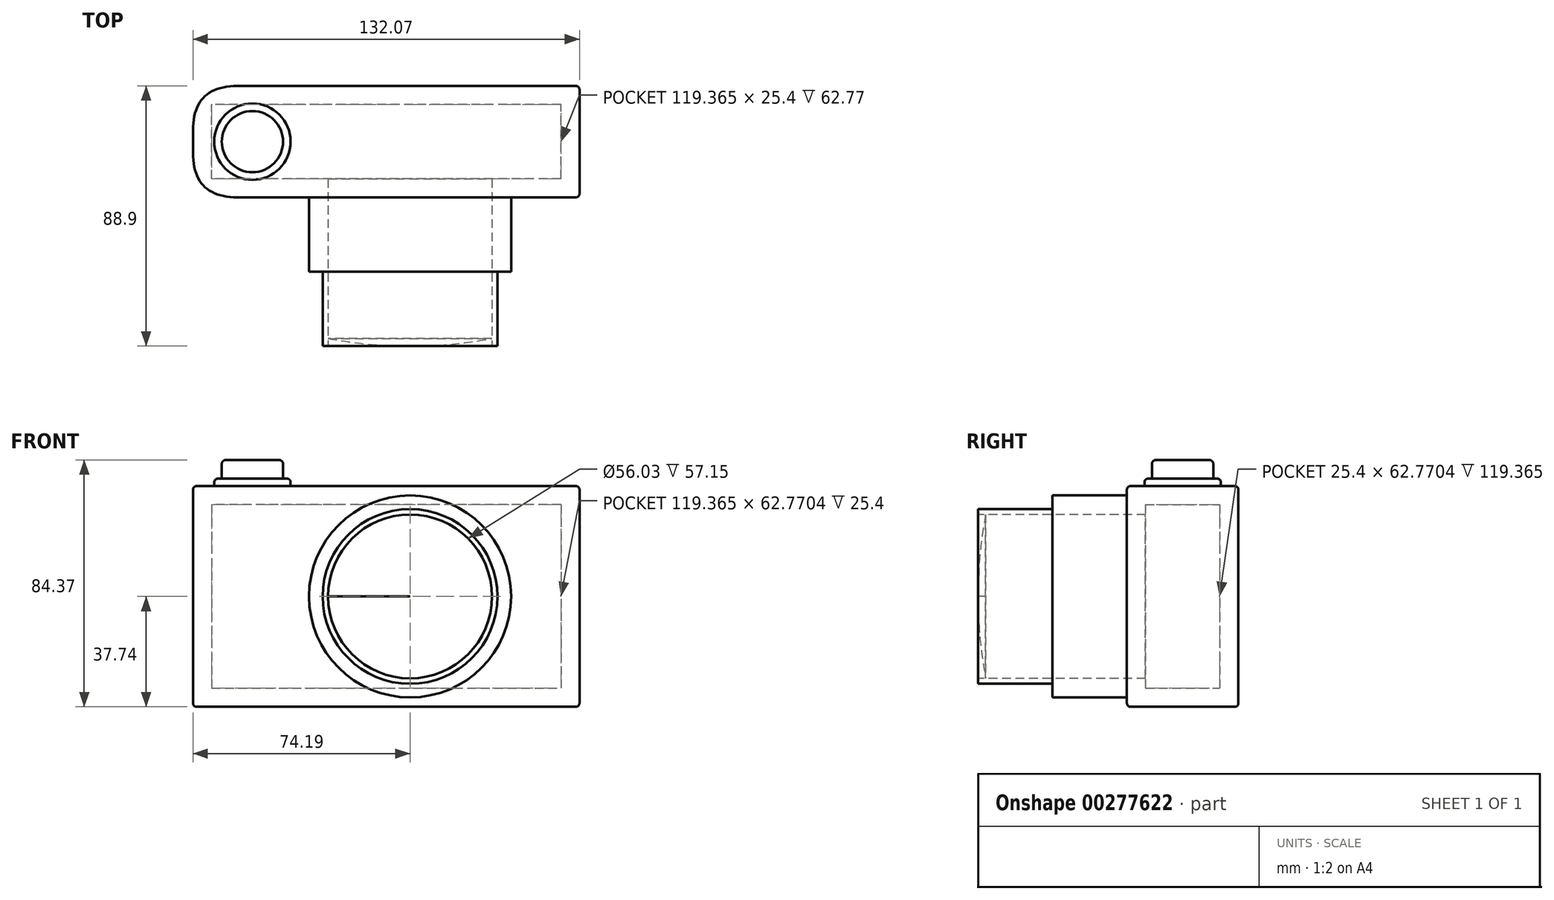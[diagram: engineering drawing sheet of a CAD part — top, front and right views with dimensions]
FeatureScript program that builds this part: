
annotation { "Feature Type Name" : "Feature", "Feature Type Description" : "" }
export const myFeature = defineFeature(function(context is Context, id is Id, definition is map)
    precondition{}
    {
        {
            var Q0;
            Q0=qCreatedBy(makeId("Front.planeOp"),FACE);
            var sketch = newSketch(context, id + "F0", { "sketchPlane" : qUnion([Q0])});
            skLineSegment(sketch, "E0.bottom", {"start": v(57.88, 37.74) * mm, "end": v(-57.88, 37.74) * mm});
            skLineSegment(sketch, "E0.top", {"start": v(57.88, -37.74) * mm, "end": v(-57.88, -37.74) * mm});
            skLineSegment(sketch, "E0.left", {"start": v(57.88, 37.74) * mm, "end": v(57.88, -37.74) * mm});
            skPoint(sketch, "E0.middle", {"position": v(0, 0) * mm});
            skCircle(sketch, "E1", {"center": v(0, 0) * mm, "radius": 34.52 * mm});
            skCircle(sketch, "E2", {"center": v(0, 0) * mm, "radius": 29.87 * mm});
            skLineSegment(sketch, "E3", {"start": v(-57.88, 37.74) * mm, "end": v(-74.19, 37.74) * mm});
            skLineSegment(sketch, "E4", {"start": v(-74.19, 37.74) * mm, "end": v(-74.19, -37.74) * mm});
            skLineSegment(sketch, "E5", {"start": v(-74.19, -37.74) * mm, "end": v(-57.88, -37.74) * mm});
            skSolve(sketch);
        }
        {
            var Q0;
            Q0 = qSketchRegion(id + "F0", true);
            var Q1;
            Q1=makeQuery(id+"F0.imprint","IMPRINT",FACE,{"disambiguationData":[TD([[makeQuery(id+"F0.imprint","IMPRINT",EDGE,{"derivedFrom":sQuery(id+"F0.wireOp",EDGE,"E1")}),1.0]])]});
            var Q2;
            Q2=makeQuery(id+"F0.imprint","IMPRINT",FACE,{"disambiguationData":[TD([[makeQuery(id+"F0.imprint","IMPRINT",EDGE,{"derivedFrom":sQuery(id+"F0.wireOp",EDGE,"E2")}),1.0]])]});
            extrude(context, id + "F1", {"entities" : qUnion([Q0, Q1, Q2]), "depth" : 38.1 * mm});
        }
        {
            var Q0;
            Q0=makeQuery(id+"F1.opExtrude","CAP_FACE",FACE,{"disambiguationData":[OSD([sQuery(id+"F0.wireOp",EDGE,"E0.bottom"),sQuery(id+"F0.wireOp",EDGE,"E0.top"),sQuery(id+"F0.wireOp",EDGE,"E0.left"),sQuery(id+"F0.wireOp",EDGE,"E3"),sQuery(id+"F0.wireOp",EDGE,"E4"),sQuery(id+"F0.wireOp",EDGE,"E5")])],"isStart":false});
            var Q1;
            Q1=makeQuery(id+"F1.opExtrude","SWEPT_BODY",BODY,{"disambiguationData":[OSD([sQuery(id+"F0.wireOp",EDGE,"E0.bottom"),sQuery(id+"F0.wireOp",EDGE,"E0.top"),sQuery(id+"F0.wireOp",EDGE,"E0.left"),sQuery(id+"F0.wireOp",EDGE,"E3"),sQuery(id+"F0.wireOp",EDGE,"E4"),sQuery(id+"F0.wireOp",EDGE,"E5")])]});
            shell(context, id + "F2", {"isHollow" : true, "entities" : qUnion([Q0]), "parts" : qUnion([Q1]), "thickness" : 6.35 * mm});
        }
        {
            var Q0;
            Q0=makeQuery(id+"F0.imprint","IMPRINT",FACE,{"disambiguationData":[TD([[makeQuery(id+"F0.imprint","IMPRINT",EDGE,{"derivedFrom":sQuery(id+"F0.wireOp",EDGE,"E1")}),1.0]])]});
            var Q1;
            Q1=makeQuery(id+"F0.imprint","IMPRINT",FACE,{"disambiguationData":[TD([[makeQuery(id+"F0.imprint","IMPRINT",EDGE,{"derivedFrom":sQuery(id+"F0.wireOp",EDGE,"E2")}),1.0]])]});
            extrude(context, id + "F3", {"entities" : qUnion([Q0, Q1]), "operationType" : NewBodyOperationType.ADD, "depth" : 63.5 * mm, "hasSecondDirection" : true, "secondDirectionOppositeDirection" : false, "secondDirectionDepth" : 38.1 * mm});
        }
        {
            var Q0;
            Q0=makeQuery(id+"F0.imprint","IMPRINT",FACE,{"disambiguationData":[TD([[makeQuery(id+"F0.imprint","IMPRINT",EDGE,{"derivedFrom":sQuery(id+"F0.wireOp",EDGE,"E2")}),1.0]])]});
            extrude(context, id + "F4", {"entities" : qUnion([Q0]), "operationType" : NewBodyOperationType.ADD, "depth" : 88.9 * mm, "hasSecondDirection" : true, "secondDirectionOppositeDirection" : false, "secondDirectionDepth" : 38.1 * mm});
        }
        {
            var Q0;
            Q0=makeQuery(id+"F1.opExtrude","SWEPT_FACE",FACE,{"disambiguationData":[OSD([sQuery(id+"F0.wireOp",EDGE,"E0.bottom"),sQuery(id+"F0.wireOp",EDGE,"E3")])]});
            var sketch = newSketch(context, id + "F5", { "sketchPlane" : qUnion([Q0])});
            skLineSegment(sketch, "E6.0", {"start": v(57.88, 0) * mm, "end": v(-74.19, 0) * mm});
            skLineSegment(sketch, "E7.0", {"start": v(-74.19, -38.1) * mm, "end": v(-74.19, 0) * mm});
            skLineSegment(sketch, "E8.0", {"start": v(57.88, -38.1) * mm, "end": v(-74.19, -38.1) * mm});
            skCircle(sketch, "E9", {"center": v(-53.87, -19.05) * mm, "radius": 13.04 * mm});
            skPoint(sketch, "E9.centerSnap0", {"position": v(-74.19, -19.05) * mm});
            skCircle(sketch, "E10", {"center": v(-53.87, -19.05) * mm, "radius": 10.45 * mm});
            skSolve(sketch);
        }
        {
            var Q0;
            Q0=makeQuery(id+"F5.imprint","IMPRINT",FACE,{"disambiguationData":[TD([[makeQuery(id+"F5.imprint","IMPRINT",EDGE,{"derivedFrom":sQuery(id+"F5.wireOp",EDGE,"E9")}),1.0]])]});
            extrude(context, id + "F6", {"entities" : qUnion([Q0]), "operationType" : NewBodyOperationType.ADD, "depth" : 2.54 * mm});
        }
        {
            var Q0;
            Q0=makeQuery(id+"F6.boolean.opBoolean","SPLIT",FACE,{"disambiguationData":[TD([makeQuery(id+"F6.opExtrude","SWEPT_FACE",FACE,{"disambiguationData":[OSD([sQuery(id+"F5.wireOp",EDGE,"E10")])]})])],"derivedFrom":makeQuery(id+"F1.opExtrude","SWEPT_FACE",FACE,{"disambiguationData":[OSD([sQuery(id+"F0.wireOp",EDGE,"E0.bottom"),sQuery(id+"F0.wireOp",EDGE,"E3")])]})});
            extrude(context, id + "F7", {"entities" : qUnion([Q0]), "operationType" : NewBodyOperationType.ADD, "depth" : 8.9 * mm});
        }
        {
            var Q0;
            Q0=makeQuery(id+"F4.opExtrude","CAP_FACE",FACE,{"disambiguationData":[OSD([sQuery(id+"F0.wireOp",EDGE,"E2")])],"isStart":false});
            var sketch = newSketch(context, id + "F8", { "sketchPlane" : qUnion([Q0])});
            skCircle(sketch, "E11", {"center": v(0, 0) * mm, "radius": 28.01 * mm});
            skSolve(sketch);
        }
        {
            var Q0;
            Q0=makeQuery(id+"F8.imprint","IMPRINT",FACE,{"disambiguationData":[TD([[makeQuery(id+"F8.imprint","IMPRINT",EDGE,{"derivedFrom":sQuery(id+"F8.wireOp",EDGE,"E11")}),1.0]])]});
            extrude(context, id + "F9", {"entities" : qUnion([Q0]), "operationType" : NewBodyOperationType.REMOVE, "oppositeDirection" : true, "depth" : 2.54 * mm});
        }
        {
            var Q0;
            Q0=qCreatedBy(makeId("Top.planeOp"),FACE);
            var sketch = newSketch(context, id + "F10", { "sketchPlane" : qUnion([Q0])});
            skLineSegment(sketch, "E12.0", {"start": v(28.01, -86.36) * mm, "end": v(-28.01, -86.36) * mm});
            skLineSegment(sketch, "E13.0", {"start": v(28.01, -88.9) * mm, "end": v(-28.01, -88.9) * mm});
            skFitSpline(sketch, "E14", {"points": [v(-28.01, -86.36) * mm, v(0, -88.9) * mm], "startDerivative": vector(28.09, -4.85) * mm, "endDerivative": vector(35.68, 0) * mm});
            skLineSegment(sketch, "E15", {"start": v(0, -88.9) * mm, "end": v(0, -86.36) * mm});
            skSolve(sketch);
        }
        {
            var Q0;
            Q0=makeQuery(id+"F8.imprint","IMPRINT",FACE,{"disambiguationData":[TD([[makeQuery(id+"F8.imprint","IMPRINT",EDGE,{"derivedFrom":sQuery(id+"F8.wireOp",EDGE,"E11")}),1.0]])]});
            extrude(context, id + "F11", {"entities" : qUnion([Q0]), "operationType" : NewBodyOperationType.REMOVE, "oppositeDirection" : true, "depth" : 63.5 * mm});
        }
        {
            var Q0;
            {var subQ0=sQuery(id+"F10.wireOp",EDGE,"E14");Q0=makeQuery(id+"F10.imprint","IMPRINT",FACE,{"disambiguationData":[TD([[makeQuery(id+"F10.imprint","IMPRINT",EDGE,{"derivedFrom":subQ0}),1.0]])]});}
            var Q1;
            Q1=sQuery(id+"F10.wireOp",EDGE,"E14");
            var Q2;
            Q2=sQuery(id+"F10.wireOp",EDGE,"E15");
            revolve(context, id + "F12", {"entities" : qUnion([Q0]), "surfaceEntities" : qUnion([Q1]), "axis" : qUnion([Q2]), "revolveType" : RevolveType.SYMMETRIC, "angle" : 360 * degree});
        }
        {
            var Q0;
            Q0=makeQuery(id+"F1.opExtrude","CAP_EDGE",EDGE,{"disambiguationData":[OSD([sQuery(id+"F0.wireOp",EDGE,"E4")])],"isStart":false});
            var Q1;
            Q1=makeQuery(id+"F1.opExtrude","CAP_EDGE",EDGE,{"disambiguationData":[OSD([sQuery(id+"F0.wireOp",EDGE,"E4")])],"isStart":true});
            fillet(context, id + "F13", {"entities" : qUnion([Q0, Q1]), "radius" : 15.24 * mm, "tangentPropagation" : true, "rho" : 0.5, "crossSection" : FilletCrossSection.CONIC, "allowEdgeOverflow" : false});
        }
        {
            var Q0;
            Q0=makeQuery(id+"F1.opExtrude","CAP_EDGE",EDGE,{"disambiguationData":[OSD([sQuery(id+"F0.wireOp",EDGE,"E0.bottom"),sQuery(id+"F0.wireOp",EDGE,"E3")])],"isStart":false});
            var Q1;
            Q1=makeQuery(id+"F1.opExtrude","SWEPT_EDGE",EDGE,{"disambiguationData":[OSD([sQuery(id+"F0.wireOp",EDGE,"E0.bottom"),sQuery(id+"F0.wireOp",EDGE,"E0.left")])]});
            var Q2;
            Q2=makeQuery(id+"F1.opExtrude","CAP_EDGE",EDGE,{"disambiguationData":[OSD([sQuery(id+"F0.wireOp",EDGE,"E0.left")])],"isStart":true});
            var Q3;
            Q3=makeQuery(id+"F1.opExtrude","CAP_EDGE",EDGE,{"disambiguationData":[OSD([sQuery(id+"F0.wireOp",EDGE,"E0.top"),sQuery(id+"F0.wireOp",EDGE,"E5")])],"isStart":true});
            var Q4;
            Q4=makeQuery(id+"F1.opExtrude","SWEPT_EDGE",EDGE,{"disambiguationData":[OSD([sQuery(id+"F0.wireOp",EDGE,"E0.top"),sQuery(id+"F0.wireOp",EDGE,"E0.left")])]});
            var Q5;
            Q5=makeQuery(id+"F1.opExtrude","CAP_EDGE",EDGE,{"disambiguationData":[OSD([sQuery(id+"F0.wireOp",EDGE,"E0.left")])],"isStart":false});
            var Q6;
            Q6=makeQuery(id+"F7.opExtrude","CAP_EDGE",EDGE,{"disambiguationData":[OSD([sQuery(id+"F5.wireOp",EDGE,"E10")])],"isStart":false});
            var Q7;
            Q7=makeQuery(id+"F6.opExtrude","CAP_EDGE",EDGE,{"disambiguationData":[OSD([sQuery(id+"F5.wireOp",EDGE,"E9")])],"isStart":false});
            fillet(context, id + "F14", {"entities" : qUnion([Q0, Q1, Q2, Q3, Q4, Q5, Q6, Q7]), "radius" : 1.27 * mm, "tangentPropagation" : true, "allowEdgeOverflow" : false});
        }
    });
